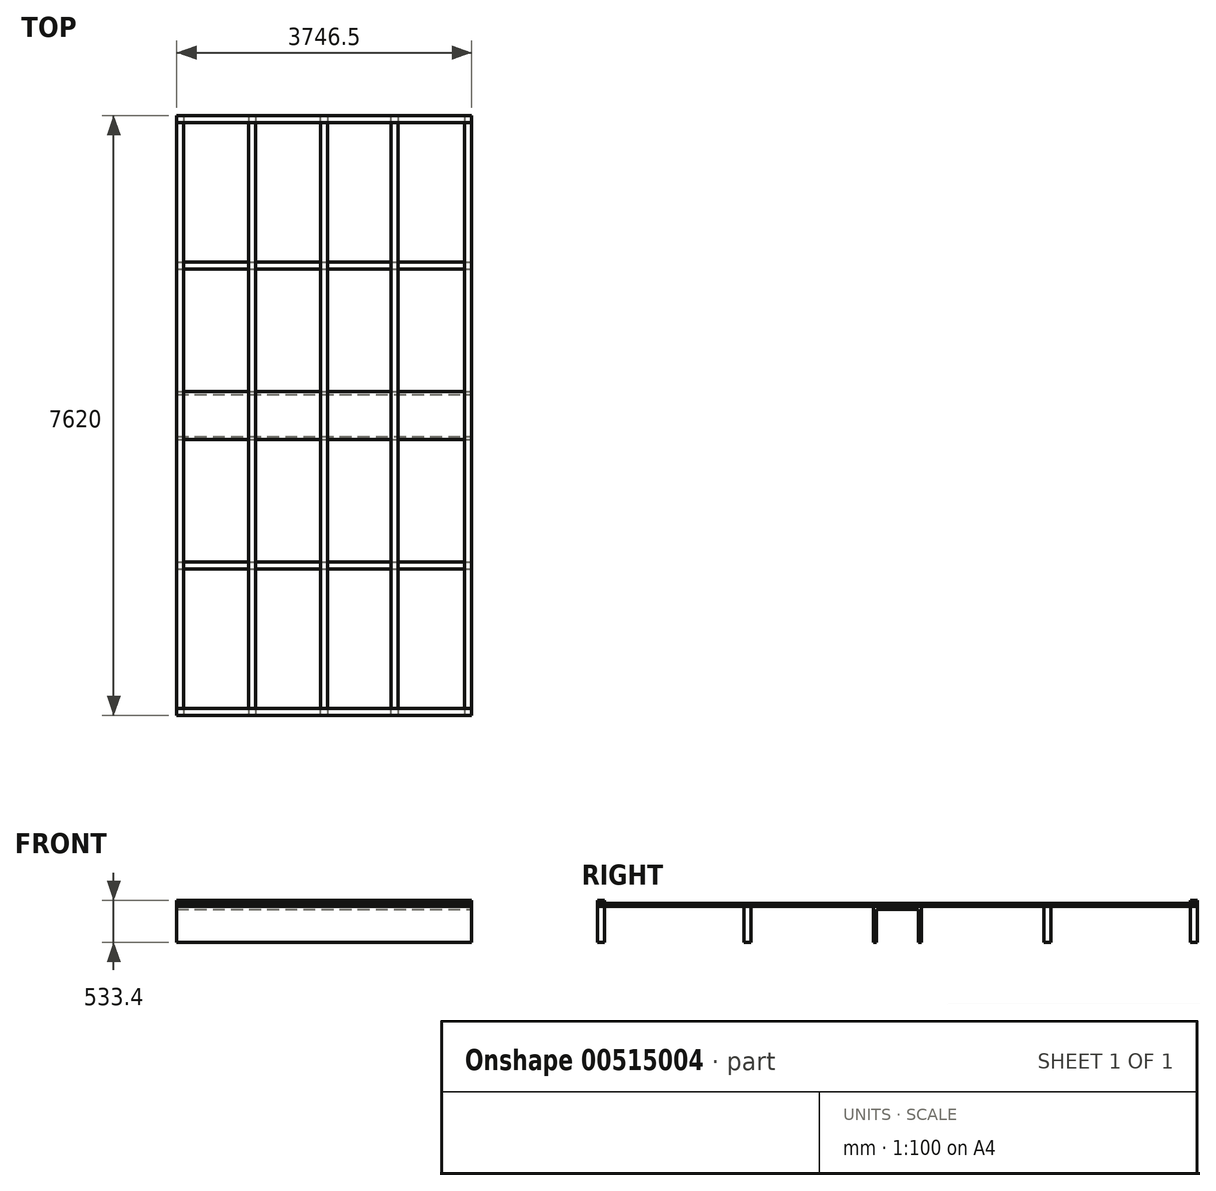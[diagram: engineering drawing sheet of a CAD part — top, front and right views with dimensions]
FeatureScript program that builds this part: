
annotation { "Feature Type Name" : "Feature", "Feature Type Description" : "" }
export const myFeature = defineFeature(function(context is Context, id is Id, definition is map)
    precondition{}
    {
        {
            var Q0;
            Q0=qCreatedBy(makeId("Top.planeOp"),FACE);
            var sketch = newSketch(context, id + "F0", { "sketchPlane" : qUnion([Q0])});
            skLineSegment(sketch, "E0", {"start": v(-1873.25, 3810) * mm, "end": v(-1784.35, 3810) * mm});
            skLineSegment(sketch, "E1", {"start": v(-959.5, 3810) * mm, "end": v(-870.6, 3810) * mm});
            skLineSegment(sketch, "E2", {"start": v(-44.45, 3810) * mm, "end": v(44.45, 3810) * mm});
            skLineSegment(sketch, "E3", {"start": v(847.72, 3810) * mm, "end": v(936.62, 3810) * mm});
            skLineSegment(sketch, "E4", {"start": v(1784.35, 3810) * mm, "end": v(1873.25, 3810) * mm});
            skLineSegment(sketch, "E5", {"start": v(-1873.25, -3810) * mm, "end": v(-1784.35, -3810) * mm});
            skLineSegment(sketch, "E6", {"start": v(-959.5, -3810) * mm, "end": v(-870.6, -3810) * mm});
            skLineSegment(sketch, "E7", {"start": v(-44.45, -3810) * mm, "end": v(44.45, -3810) * mm});
            skLineSegment(sketch, "E8", {"start": v(847.73, -3810) * mm, "end": v(936.62, -3810) * mm});
            skLineSegment(sketch, "E9", {"start": v(1873.25, -3810) * mm, "end": v(1784.35, -3810) * mm});
            skLineSegment(sketch, "E10", {"start": v(-1873.25, 0) * mm, "end": v(-1784.35, 0) * mm});
            skLineSegment(sketch, "E11.trimOffspring", {"start": v(-959.5, 0) * mm, "end": v(-870.6, 0) * mm});
            skLineSegment(sketch, "E12.trimOffspring", {"start": v(-44.45, 0) * mm, "end": v(44.45, 0) * mm});
            skLineSegment(sketch, "E13.trimOffspring", {"start": v(847.72, 0) * mm, "end": v(936.62, 0) * mm});
            skLineSegment(sketch, "E14.trimOffspring", {"start": v(1784.35, 0) * mm, "end": v(1873.25, 0) * mm});
            skLineSegment(sketch, "E15", {"start": v(-1873.25, -1905) * mm, "end": v(-1784.35, -1905) * mm});
            skLineSegment(sketch, "E16", {"start": v(-1873.25, -3810) * mm, "end": v(-1873.25, -1905) * mm});
            skLineSegment(sketch, "E17", {"start": v(-1873.25, 0) * mm, "end": v(-1873.25, -1905) * mm});
            skLineSegment(sketch, "E18", {"start": v(-1784.35, 0) * mm, "end": v(-1784.35, -1905) * mm});
            skLineSegment(sketch, "E19", {"start": v(-1784.35, -1905) * mm, "end": v(-1784.35, -3810) * mm});
            skLineSegment(sketch, "E20", {"start": v(-959.5, -3810) * mm, "end": v(-959.5, -1905) * mm});
            skLineSegment(sketch, "E21", {"start": v(-959.5, -1905) * mm, "end": v(-959.5, 0) * mm});
            skLineSegment(sketch, "E22", {"start": v(-870.6, 0) * mm, "end": v(-870.6, -1905) * mm});
            skLineSegment(sketch, "E23", {"start": v(-870.6, -1905) * mm, "end": v(-870.6, -3810) * mm});
            skLineSegment(sketch, "E24", {"start": v(-44.45, -3810) * mm, "end": v(-44.45, -1905) * mm});
            skLineSegment(sketch, "E25", {"start": v(-44.45, -1905) * mm, "end": v(-44.45, 0) * mm});
            skLineSegment(sketch, "E26", {"start": v(44.45, 0) * mm, "end": v(44.45, -1905) * mm});
            skLineSegment(sketch, "E27", {"start": v(44.45, -1905) * mm, "end": v(44.45, -3810) * mm});
            skLineSegment(sketch, "E28", {"start": v(847.73, -3810) * mm, "end": v(847.73, -1905) * mm});
            skLineSegment(sketch, "E29", {"start": v(847.73, -1905) * mm, "end": v(847.72, 0) * mm});
            skLineSegment(sketch, "E30", {"start": v(936.62, 0) * mm, "end": v(936.62, -1905) * mm});
            skLineSegment(sketch, "E31", {"start": v(936.62, -1905) * mm, "end": v(936.62, -3810) * mm});
            skLineSegment(sketch, "E32", {"start": v(1784.35, -3810) * mm, "end": v(1784.35, -1905) * mm});
            skLineSegment(sketch, "E33", {"start": v(1784.35, -1905) * mm, "end": v(1784.35, 0) * mm});
            skLineSegment(sketch, "E34", {"start": v(1873.25, 0) * mm, "end": v(1873.25, -1905) * mm});
            skLineSegment(sketch, "E35", {"start": v(1873.25, -1905) * mm, "end": v(1873.25, -3810) * mm});
            skLineSegment(sketch, "E36", {"start": v(1873.25, 0) * mm, "end": v(1873.25, 1905) * mm});
            skLineSegment(sketch, "E37", {"start": v(1873.25, 1905) * mm, "end": v(1784.35, 1905) * mm});
            skLineSegment(sketch, "E38", {"start": v(-1873.25, 0) * mm, "end": v(-1873.25, 1905) * mm});
            skLineSegment(sketch, "E39", {"start": v(-1873.25, 3810) * mm, "end": v(-1873.25, 1905) * mm});
            skLineSegment(sketch, "E40", {"start": v(-1784.35, 3810) * mm, "end": v(-1784.35, 1905) * mm});
            skLineSegment(sketch, "E41", {"start": v(-1784.35, 1905) * mm, "end": v(-1784.35, 0) * mm});
            skLineSegment(sketch, "E42", {"start": v(-959.5, 0) * mm, "end": v(-959.5, 1905) * mm});
            skLineSegment(sketch, "E43", {"start": v(-959.5, 3810) * mm, "end": v(-959.5, 1905) * mm});
            skLineSegment(sketch, "E44", {"start": v(-870.6, 3810) * mm, "end": v(-870.6, 1905) * mm});
            skLineSegment(sketch, "E45", {"start": v(-870.6, 1905) * mm, "end": v(-870.6, 0) * mm});
            skLineSegment(sketch, "E46", {"start": v(-44.45, 0) * mm, "end": v(-44.45, 1905) * mm});
            skLineSegment(sketch, "E47", {"start": v(-44.45, 1905) * mm, "end": v(-44.45, 3810) * mm});
            skLineSegment(sketch, "E48", {"start": v(44.45, 3810) * mm, "end": v(44.45, 1905) * mm});
            skLineSegment(sketch, "E49", {"start": v(44.45, 1905) * mm, "end": v(44.45, 0) * mm});
            skLineSegment(sketch, "E50", {"start": v(847.72, 0) * mm, "end": v(847.72, 1905) * mm});
            skLineSegment(sketch, "E51", {"start": v(936.62, 3810) * mm, "end": v(936.62, 1905) * mm});
            skLineSegment(sketch, "E52", {"start": v(936.62, 1905) * mm, "end": v(936.62, 0) * mm});
            skLineSegment(sketch, "E53", {"start": v(847.73, 1905) * mm, "end": v(847.72, 3810) * mm});
            skLineSegment(sketch, "E54", {"start": v(1873.25, 3810) * mm, "end": v(1873.25, 1905) * mm});
            skLineSegment(sketch, "E55", {"start": v(1784.35, 3810) * mm, "end": v(1784.35, 1905) * mm});
            skLineSegment(sketch, "E56", {"start": v(1784.35, 1905) * mm, "end": v(1784.35, 0) * mm});
            skLineSegment(sketch, "E57.trimOffspring", {"start": v(-1784.35, 1905) * mm, "end": v(-1873.25, 1905) * mm});
            skLineSegment(sketch, "E58.trimOffspring", {"start": v(-870.6, 1905) * mm, "end": v(-959.5, 1905) * mm});
            skLineSegment(sketch, "E59.trimOffspring", {"start": v(44.45, 1905) * mm, "end": v(-44.45, 1905) * mm});
            skLineSegment(sketch, "E60.trimOffspring", {"start": v(936.62, 1905) * mm, "end": v(847.73, 1905) * mm});
            skLineSegment(sketch, "E61.trimOffspring", {"start": v(1784.35, -1905) * mm, "end": v(1873.25, -1905) * mm});
            skLineSegment(sketch, "E62.trimOffspring", {"start": v(847.73, -1905) * mm, "end": v(936.62, -1905) * mm});
            skLineSegment(sketch, "E63.trimOffspring", {"start": v(-44.45, -1905) * mm, "end": v(44.45, -1905) * mm});
            skLineSegment(sketch, "E64.trimOffspring", {"start": v(-959.5, -1905) * mm, "end": v(-870.6, -1905) * mm});
            skSolve(sketch);
        }
        {
            var Q0;
            Q0 = qSketchRegion(id + "F0", true);
            extrude(context, id + "F1", {"entities" : qUnion([Q0]), "oppositeDirection" : true, "depth" : 38.1 * mm, "offsetDistance" : 25.4 * mm});
        }
        {
            var Q0;
            Q0=makeQuery(id+"F1.opExtrude","CAP_FACE",FACE,{"disambiguationData":[OSD([sQuery(id+"F0.wireOp",EDGE,"907U57ns-8viv-Dxdj-WWCM-g9XBL40LAbgK.left"),sQuery(id+"F0.wireOp",EDGE,"907U57ns-8viv-Dxdj-WWCM-g9XBL40LAbgK.right"),sQuery(id+"F0.wireOp",EDGE,"E0"),sQuery(id+"F0.wireOp",EDGE,"E5")])],"isStart":true});
            var sketch = newSketch(context, id + "F2", { "sketchPlane" : qUnion([Q0])});
            skLineSegment(sketch, "E65.bottom", {"start": v(-1873.25, 3810) * mm, "end": v(1873.25, 3810) * mm});
            skLineSegment(sketch, "E65.top", {"start": v(-1873.25, 3721.1) * mm, "end": v(1873.25, 3721.1) * mm});
            skLineSegment(sketch, "E65.left", {"start": v(-1873.25, 3810) * mm, "end": v(-1873.25, 3721.1) * mm});
            skLineSegment(sketch, "E65.right", {"start": v(1873.25, 3810) * mm, "end": v(1873.25, 3721.1) * mm});
            skLineSegment(sketch, "E66.bottom", {"start": v(-1873.25, -3810) * mm, "end": v(1873.25, -3810) * mm});
            skLineSegment(sketch, "E66.top", {"start": v(-1873.25, -3721.1) * mm, "end": v(1873.25, -3721.1) * mm});
            skLineSegment(sketch, "E66.left", {"start": v(-1873.25, -3810) * mm, "end": v(-1873.25, -3721.1) * mm});
            skLineSegment(sketch, "E66.right", {"start": v(1873.25, -3810) * mm, "end": v(1873.25, -3721.1) * mm});
            skSolve(sketch);
        }
        {
            var Q0;
            Q0 = qSketchRegion(id + "F2", true);
            extrude(context, id + "F3", {"entities" : qUnion([Q0]), "depth" : 38.1 * mm, "offsetDistance" : 25.4 * mm});
        }
        {
            var Q0;
            Q0=makeQuery(id+"F1.opExtrude","SWEPT_FACE",FACE,{"disambiguationData":[OSD([sQuery(id+"F0.wireOp",EDGE,"E34"),sQuery(id+"F0.wireOp",EDGE,"E35"),sQuery(id+"F0.wireOp",EDGE,"E36"),sQuery(id+"F0.wireOp",EDGE,"E54")])]});
            var sketch = newSketch(context, id + "F4", { "sketchPlane" : qUnion([Q0])});
            skLineSegment(sketch, "E67.right", {"start": v(304.8, -38.1) * mm, "end": v(304.8, -76.2) * mm});
            skLineSegment(sketch, "E68.right", {"start": v(-304.8, -76.2) * mm, "end": v(-304.8, -38.1) * mm});
            skLineSegment(sketch, "E69.top", {"start": v(-304.8, -38.1) * mm, "end": v(304.8, -38.1) * mm});
            skLineSegment(sketch, "E69.right", {"start": v(304.8, -76.2) * mm, "end": v(304.8, -38.1) * mm});
            skLineSegment(sketch, "E70", {"start": v(-304.8, -76.2) * mm, "end": v(304.8, -76.2) * mm});
            skLineSegment(sketch, "E71.bottom", {"start": v(304.8, -76.2) * mm, "end": v(266.7, -76.2) * mm});
            skLineSegment(sketch, "E71.top", {"start": v(304.8, -495.3) * mm, "end": v(266.7, -495.3) * mm});
            skLineSegment(sketch, "E71.left", {"start": v(304.8, -76.2) * mm, "end": v(304.8, -495.3) * mm});
            skLineSegment(sketch, "E71.right", {"start": v(266.7, -76.2) * mm, "end": v(266.7, -495.3) * mm});
            skLineSegment(sketch, "E72.top", {"start": v(266.7, -76.2) * mm, "end": v(-304.8, -76.2) * mm});
            skLineSegment(sketch, "E72.left", {"start": v(266.7, -495.3) * mm, "end": v(266.7, -76.2) * mm});
            skLineSegment(sketch, "E72.right", {"start": v(-304.8, -495.3) * mm, "end": v(-304.8, -76.2) * mm});
            skLineSegment(sketch, "E73.bottom", {"start": v(-304.8, -495.3) * mm, "end": v(-266.7, -495.3) * mm});
            skLineSegment(sketch, "E73.top", {"start": v(-304.8, -76.2) * mm, "end": v(-266.7, -76.2) * mm});
            skLineSegment(sketch, "E73.right", {"start": v(-266.7, -495.3) * mm, "end": v(-266.7, -76.2) * mm});
            skLineSegment(sketch, "E74.bottom", {"start": v(3810, -38.1) * mm, "end": v(3721.1, -38.1) * mm});
            skLineSegment(sketch, "E74.top", {"start": v(3810, -495.3) * mm, "end": v(3721.1, -495.3) * mm});
            skLineSegment(sketch, "E74.left", {"start": v(3810, -38.1) * mm, "end": v(3810, -495.3) * mm});
            skLineSegment(sketch, "E74.right", {"start": v(3721.1, -38.1) * mm, "end": v(3721.1, -495.3) * mm});
            skLineSegment(sketch, "E75.bottom", {"start": v(-3810, -38.1) * mm, "end": v(-3721.1, -38.1) * mm});
            skLineSegment(sketch, "E75.top", {"start": v(-3810, -495.3) * mm, "end": v(-3721.1, -495.3) * mm});
            skLineSegment(sketch, "E75.left", {"start": v(-3810, -38.1) * mm, "end": v(-3810, -495.3) * mm});
            skLineSegment(sketch, "E75.right", {"start": v(-3721.1, -38.1) * mm, "end": v(-3721.1, -495.3) * mm});
            skLineSegment(sketch, "E76", {"start": v(3810, -38.1) * mm, "end": v(0, -38.1) * mm});
            skLineSegment(sketch, "E77", {"start": v(0, -38.1) * mm, "end": v(-3810, -38.1) * mm});
            skLineSegment(sketch, "E78.top", {"start": v(1860.55, -495.3) * mm, "end": v(1949.45, -495.3) * mm});
            skLineSegment(sketch, "E78.left", {"start": v(1860.55, -38.1) * mm, "end": v(1860.55, -495.3) * mm});
            skLineSegment(sketch, "E78.right", {"start": v(1949.45, -38.1) * mm, "end": v(1949.45, -495.3) * mm});
            skLineSegment(sketch, "E79", {"start": v(1949.45, -38.1) * mm, "end": v(1860.55, -38.1) * mm});
            skLineSegment(sketch, "E80.bottom", {"start": v(-1949.45, -38.1) * mm, "end": v(-1860.55, -38.1) * mm});
            skLineSegment(sketch, "E80.top", {"start": v(-1949.45, -495.3) * mm, "end": v(-1860.55, -495.3) * mm});
            skLineSegment(sketch, "E80.left", {"start": v(-1949.45, -38.1) * mm, "end": v(-1949.45, -495.3) * mm});
            skLineSegment(sketch, "E80.right", {"start": v(-1860.55, -38.1) * mm, "end": v(-1860.55, -495.3) * mm});
            skSolve(sketch);
        }
        {
            var Q0;
            Q0 = qSketchRegion(id + "F4", true);
            extrude(context, id + "F5", {"entities" : qUnion([Q0]), "oppositeDirection" : true, "depth" : 3746.5 * mm, "offsetDistance" : 25.4 * mm});
        }
    });
